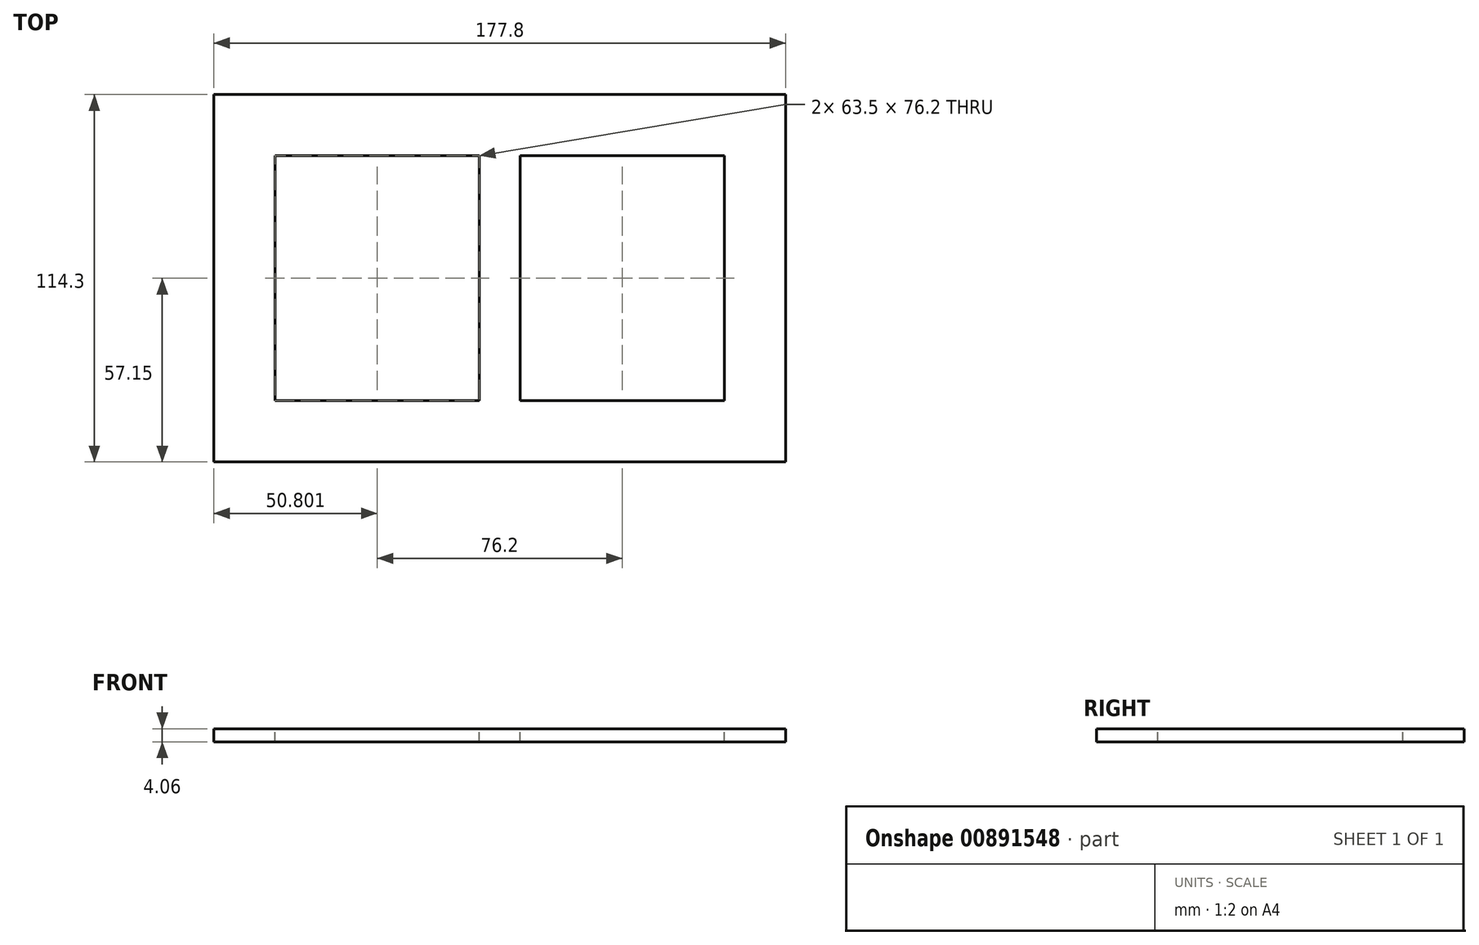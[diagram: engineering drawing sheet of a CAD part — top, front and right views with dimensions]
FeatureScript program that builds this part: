
annotation { "Feature Type Name" : "Feature", "Feature Type Description" : "" }
export const myFeature = defineFeature(function(context is Context, id is Id, definition is map)
    precondition{}
    {
        {
            var Q0;
            Q0=qCreatedBy(makeId("Top.planeOp"),FACE);
            var sketch = newSketch(context, id + "F0", { "sketchPlane" : qUnion([Q0])});
            skLineSegment(sketch, "E0.bottom", {"start": v(-87.1, 55.14) * mm, "end": v(90.7, 55.14) * mm});
            skLineSegment(sketch, "E0.top", {"start": v(-87.1, -59.16) * mm, "end": v(90.7, -59.16) * mm});
            skLineSegment(sketch, "E0.left", {"start": v(-87.1, 55.14) * mm, "end": v(-87.1, -59.16) * mm});
            skLineSegment(sketch, "E0.right", {"start": v(90.7, 55.14) * mm, "end": v(90.7, -59.16) * mm});
            skSolve(sketch);
        }
        {
            var Q0;
            Q0 = qSketchRegion(id + "F0", true);
            extrude(context, id + "F1", {"entities" : qUnion([Q0]), "depth" : 4.06 * mm, "offsetDistance" : 25.4 * mm});
        }
        {
            var Q0;
            Q0=makeQuery(id+"F1.opExtrude","CAP_FACE",FACE,{"disambiguationData":[OSD([sQuery(id+"F0.wireOp",EDGE,"E0.bottom"),sQuery(id+"F0.wireOp",EDGE,"E0.top"),sQuery(id+"F0.wireOp",EDGE,"E0.left"),sQuery(id+"F0.wireOp",EDGE,"E0.right")])],"isStart":false});
            var sketch = newSketch(context, id + "F2", { "sketchPlane" : qUnion([Q0])});
            skLineSegment(sketch, "E1.bottom", {"start": v(-68.05, 36.1) * mm, "end": v(71.65, 36.1) * mm});
            skLineSegment(sketch, "E1.top", {"start": v(-68.05, -40.1) * mm, "end": v(71.65, -40.1) * mm});
            skLineSegment(sketch, "E1.left", {"start": v(-68.05, 36.1) * mm, "end": v(-68.05, -40.1) * mm});
            skLineSegment(sketch, "E1.right", {"start": v(71.65, 36.1) * mm, "end": v(71.65, -40.1) * mm});
            skLineSegment(sketch, "E2.bottom", {"start": v(-4.55, 55.14) * mm, "end": v(8.15, 55.14) * mm});
            skLineSegment(sketch, "E2.top", {"start": v(-4.55, -59.16) * mm, "end": v(8.15, -59.16) * mm});
            skLineSegment(sketch, "E2.left", {"start": v(-4.55, 55.14) * mm, "end": v(-4.55, -59.16) * mm});
            skLineSegment(sketch, "E2.right", {"start": v(8.15, 55.14) * mm, "end": v(8.15, -59.16) * mm});
            skSolve(sketch);
        }
        {
            var Q0;
            {var subQ0=sQuery(id+"F2.wireOp",EDGE,"E1.left");Q0=makeQuery(id+"F2.imprint","IMPRINT",FACE,{"disambiguationData":[TD([[makeQuery(id+"F2.imprint","IMPRINT",EDGE,{"derivedFrom":subQ0}),1.0]])]});}
            var Q1;
            {var subQ0=sQuery(id+"F2.wireOp",EDGE,"E1.right");Q1=makeQuery(id+"F2.imprint","IMPRINT",FACE,{"disambiguationData":[TD([[makeQuery(id+"F2.imprint","IMPRINT",EDGE,{"derivedFrom":subQ0}),-1.0]])]});}
            extrude(context, id + "F3", {"entities" : qUnion([Q0, Q1]), "operationType" : NewBodyOperationType.REMOVE, "oppositeDirection" : true, "depth" : 4.06 * mm, "offsetDistance" : 25.4 * mm});
        }
    });
